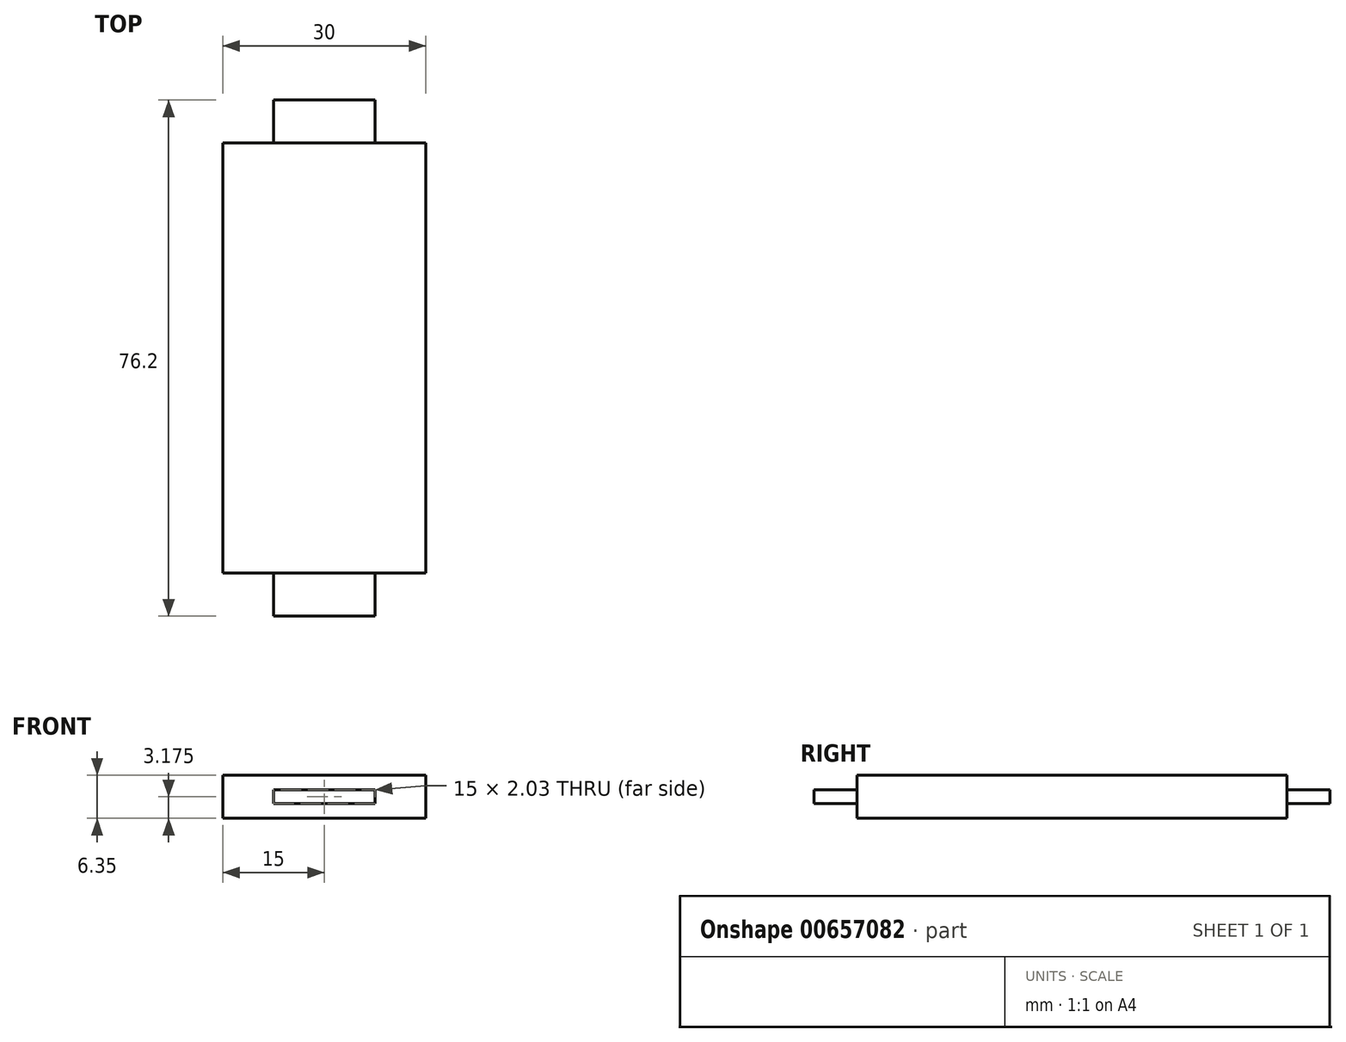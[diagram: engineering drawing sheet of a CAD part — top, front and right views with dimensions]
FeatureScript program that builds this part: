
annotation { "Feature Type Name" : "Feature", "Feature Type Description" : "" }
export const myFeature = defineFeature(function(context is Context, id is Id, definition is map)
    precondition{}
    {
        {
            var Q0;
            Q0=qCreatedBy(makeId("Front.planeOp"),FACE);
            var sketch = newSketch(context, id + "F0", { "sketchPlane" : qUnion([Q0])});
            skLineSegment(sketch, "E0.bottom", {"start": v(0, 0) * mm, "end": v(30, 0) * mm});
            skLineSegment(sketch, "E0.top", {"start": v(0, 6.35) * mm, "end": v(30, 6.35) * mm});
            skLineSegment(sketch, "E0.left", {"start": v(0, 0) * mm, "end": v(0, 6.35) * mm});
            skLineSegment(sketch, "E0.right", {"start": v(30, 0) * mm, "end": v(30, 6.35) * mm});
            skLineSegment(sketch, "E1.bottom", {"start": v(7.5, 4.2) * mm, "end": v(22.5, 4.2) * mm});
            skLineSegment(sketch, "E1.top", {"start": v(7.5, 2.16) * mm, "end": v(22.5, 2.16) * mm});
            skLineSegment(sketch, "E1.left", {"start": v(7.5, 4.2) * mm, "end": v(7.5, 2.16) * mm});
            skLineSegment(sketch, "E1.right", {"start": v(22.5, 4.2) * mm, "end": v(22.5, 2.16) * mm});
            skLineSegment(sketch, "E2", {"start": v(13.8, 6.35) * mm, "end": v(13.8, 4.2) * mm});
            skLineSegment(sketch, "E3", {"start": v(13.91, 2.16) * mm, "end": v(13.91, 0) * mm});
            skLineSegment(sketch, "E4", {"start": v(0, 3.17) * mm, "end": v(7.5, 3.18) * mm});
            skLineSegment(sketch, "E5", {"start": v(22.5, 3.18) * mm, "end": v(30, 3.18) * mm});
            skSolve(sketch);
        }
        {
            var Q0;
            {var subQ7=sQuery(id+"F0.wireOp",EDGE,"E3");Q0=makeQuery(id+"F0.imprint","IMPRINT",FACE,{"disambiguationData":[TD([[makeQuery(id+"F0.imprint","IMPRINT",EDGE,{"derivedFrom":subQ7}),-1.0]])]});}
            var Q1;
            {var subQ4=sQuery(id+"F0.wireOp",EDGE,"E3");Q1=makeQuery(id+"F0.imprint","IMPRINT",FACE,{"disambiguationData":[TD([[makeQuery(id+"F0.imprint","IMPRINT",EDGE,{"derivedFrom":subQ4}),1.0]])]});}
            var Q2;
            {var subQ7=sQuery(id+"F0.wireOp",EDGE,"E2");Q2=makeQuery(id+"F0.imprint","IMPRINT",FACE,{"disambiguationData":[TD([[makeQuery(id+"F0.imprint","IMPRINT",EDGE,{"derivedFrom":subQ7}),1.0]])]});}
            var Q3;
            {var subQ3=sQuery(id+"F0.wireOp",EDGE,"E2");Q3=makeQuery(id+"F0.imprint","IMPRINT",FACE,{"disambiguationData":[TD([[makeQuery(id+"F0.imprint","IMPRINT",EDGE,{"derivedFrom":subQ3}),-1.0]])]});}
            extrude(context, id + "F1", {"entities" : qUnion([Q0, Q1, Q2, Q3]), "depth" : 69.85 * mm, "offsetDistance" : 25.4 * mm, "hasSecondDirection" : true, "secondDirectionOppositeDirection" : true, "secondDirectionDepth" : -6.35 * mm});
        }
        {
            var Q0;
            {var subQ4=sQuery(id+"F0.wireOp",EDGE,"E1.left");var subQ6=sQuery(id+"F0.wireOp",EDGE,"E1.bottom");var subQ9=makeQuery(id+"F0.imprint","INTERSECT",VERTEX,{"derivedFrom":[subQ6,subQ4]});Q0=makeQuery(id+"F0.imprint","IMPRINT",FACE,{"disambiguationData":[TD([[makeQuery(id+"F0.imprint","IMPRINT",EDGE,{"disambiguationData":[TD([[subQ9,-1.0]])],"derivedFrom":subQ6}),-1.0]])]});}
            extrude(context, id + "F2", {"entities" : qUnion([Q0]), "operationType" : NewBodyOperationType.ADD, "depth" : 76.2 * mm, "offsetDistance" : 25.4 * mm});
        }
    });
